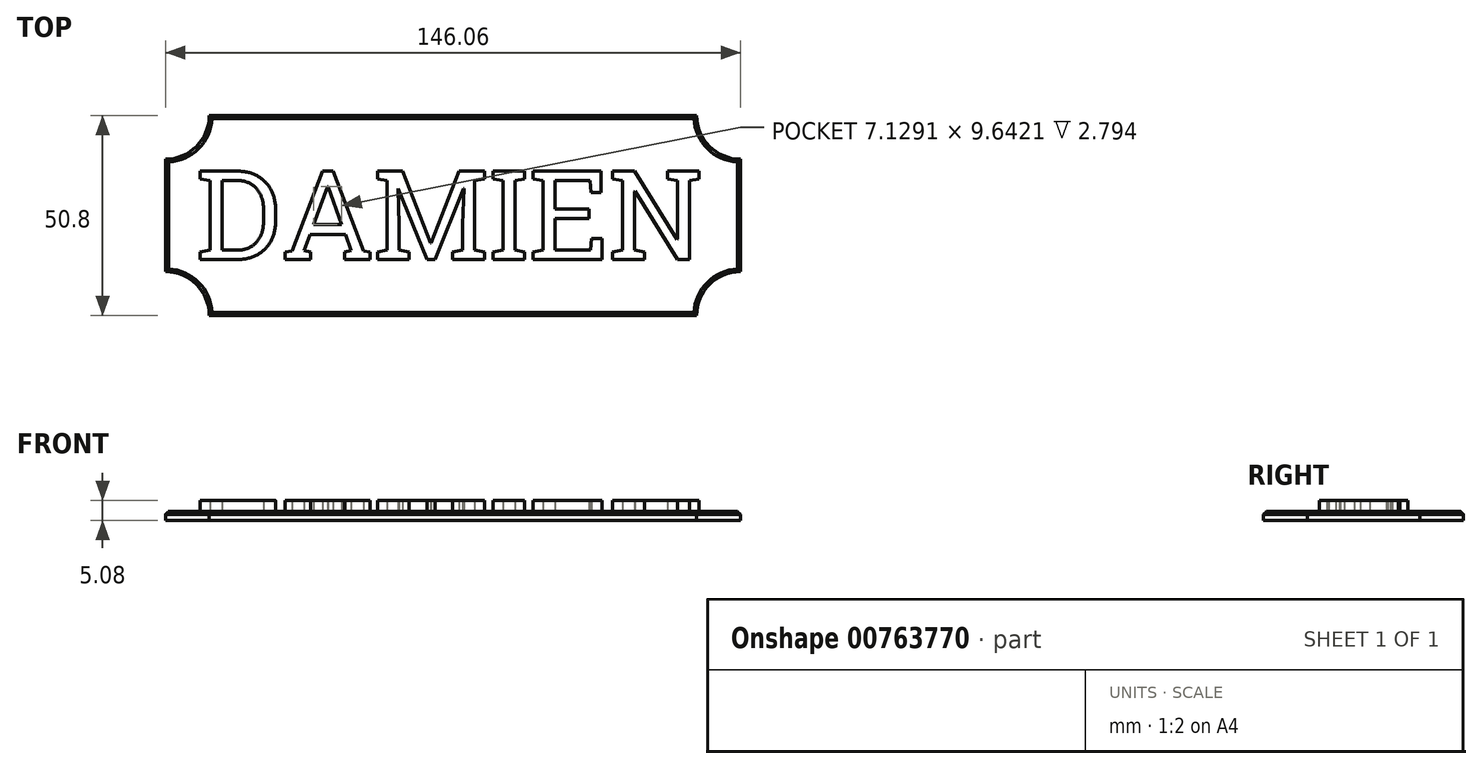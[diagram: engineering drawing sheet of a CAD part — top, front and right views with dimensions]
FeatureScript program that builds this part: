
annotation { "Feature Type Name" : "Feature", "Feature Type Description" : "" }
export const myFeature = defineFeature(function(context is Context, id is Id, definition is map)
    precondition{}
    {
        {
            var Q0;
            Q0=qCreatedBy(makeId("Top.planeOp"),FACE);
            var sketch = newSketch(context, id + "F0", { "sketchPlane" : qUnion([Q0])});
            skLineSegment(sketch, "E0.bottom", {"start": v(61.91, -25.4) * mm, "end": v(-61.91, -25.4) * mm});
            skLineSegment(sketch, "E0.top", {"start": v(61.91, 25.4) * mm, "end": v(-61.91, 25.4) * mm});
            skLineSegment(sketch, "E0.left", {"start": v(73.03, -14.29) * mm, "end": v(73.03, 14.29) * mm});
            skLineSegment(sketch, "E0.right", {"start": v(-73.03, -14.29) * mm, "end": v(-73.03, 14.29) * mm});
            skPoint(sketch, "E0.middle", {"position": v(0, 0) * mm});
            skArc(sketch, "E1", {"start": v(-73.03, 14.29) * mm, "mid": v(-65.17, 17.54) * mm, "end": v(-61.91, 25.4) * mm});
            skArc(sketch, "E2", {"start": v(61.91, 25.4) * mm, "mid": v(65.17, 17.54) * mm, "end": v(73.03, 14.29) * mm});
            skArc(sketch, "E3", {"start": v(73.03, -14.29) * mm, "mid": v(65.17, -17.54) * mm, "end": v(61.91, -25.4) * mm});
            skArc(sketch, "E4", {"start": v(-61.91, -25.4) * mm, "mid": v(-65.17, -17.54) * mm, "end": v(-73.03, -14.29) * mm});
            skSolve(sketch);
        }
        {
            var Q0;
            Q0=qCreatedBy(makeId("Top.planeOp"),FACE);
            var sketch = newSketch(context, id + "F1", { "sketchPlane" : qUnion([Q0])});
            skText(sketch, "E5", { "text": "DAMIEN", "fontName": "RobotoSlab-Regular.ttf"});
            const initialGuessF1  = {"E5": [-0.06534, -0.0112, 1, 0, 0.02275]};
            skSetInitialGuess(sketch, initialGuessF1);
            skSolve(sketch);
        }
        {
            var Q0;
            Q0 = qSketchRegion(id + "F0", true);
            extrude(context, id + "F2", {"entities" : qUnion([Q0]), "depth" : 2.3 * mm, "offsetDistance" : 25.4 * mm});
        }
        {
            var Q0;
            Q0 = qSketchRegion(id + "F1", true);
            extrude(context, id + "F3", {"entities" : qUnion([Q0]), "operationType" : NewBodyOperationType.ADD, "depth" : 5.08 * mm, "offsetDistance" : 25.4 * mm});
        }
        {
            var Q0;
            Q0=makeQuery(id+"F2.opExtrude","CAP_EDGE",EDGE,{"disambiguationData":[OSD([sQuery(id+"F0.wireOp",EDGE,"E0.right")])],"isStart":false});
            var Q1;
            Q1=makeQuery(id+"F2.opExtrude","CAP_EDGE",EDGE,{"disambiguationData":[OSD([sQuery(id+"F0.wireOp",EDGE,"E1")])],"isStart":false});
            var Q2;
            Q2=makeQuery(id+"F2.opExtrude","CAP_EDGE",EDGE,{"disambiguationData":[OSD([sQuery(id+"F0.wireOp",EDGE,"E0.left")])],"isStart":false});
            var Q3;
            Q3=makeQuery(id+"F2.opExtrude","CAP_EDGE",EDGE,{"disambiguationData":[OSD([sQuery(id+"F0.wireOp",EDGE,"E2")])],"isStart":false});
            var Q4;
            Q4=makeQuery(id+"F2.opExtrude","CAP_EDGE",EDGE,{"disambiguationData":[OSD([sQuery(id+"F0.wireOp",EDGE,"E0.top")])],"isStart":false});
            var Q5;
            Q5=makeQuery(id+"F2.opExtrude","CAP_EDGE",EDGE,{"disambiguationData":[OSD([sQuery(id+"F0.wireOp",EDGE,"E4")])],"isStart":false});
            var Q6;
            Q6=makeQuery(id+"F2.opExtrude","CAP_EDGE",EDGE,{"disambiguationData":[OSD([sQuery(id+"F0.wireOp",EDGE,"E0.bottom")])],"isStart":false});
            var Q7;
            Q7=makeQuery(id+"F2.opExtrude","CAP_EDGE",EDGE,{"disambiguationData":[OSD([sQuery(id+"F0.wireOp",EDGE,"E3")])],"isStart":false});
            chamfer(context, id + "F4", {"entities" : qUnion([Q0, Q1, Q2, Q3, Q4, Q5, Q6, Q7]), "width" : 0.76 * mm, "tangentPropagation" : true});
        }
    });
